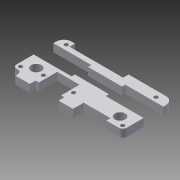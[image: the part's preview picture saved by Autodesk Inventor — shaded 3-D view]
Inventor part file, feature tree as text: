
AUTODESK INVENTOR PART (.ipt)
format: ipt  version: 2013 (Build 170138000, 138)  size: 138,240 bytes
history: native  units: mm
features: extrude x1, sketch x1
ambient origin geometry x8: Origin, YZ Plane, XZ Plane, XY Plane, X Axis, Y Axis, Z Axis, Center Point
bodies: Solid1 (feature_tree)
feature tree (2):
  extrude  "Extrusion1"  [1 undecoded]
  sketch  "Sketch1"  dims[d0=6.0mm d1=0.0mm]
note: 1 required parameter value undecoded (feature->parameter linkage not recoverable at this tier; creation-order binding heuristic only, values carry confidence <= 0.55)
